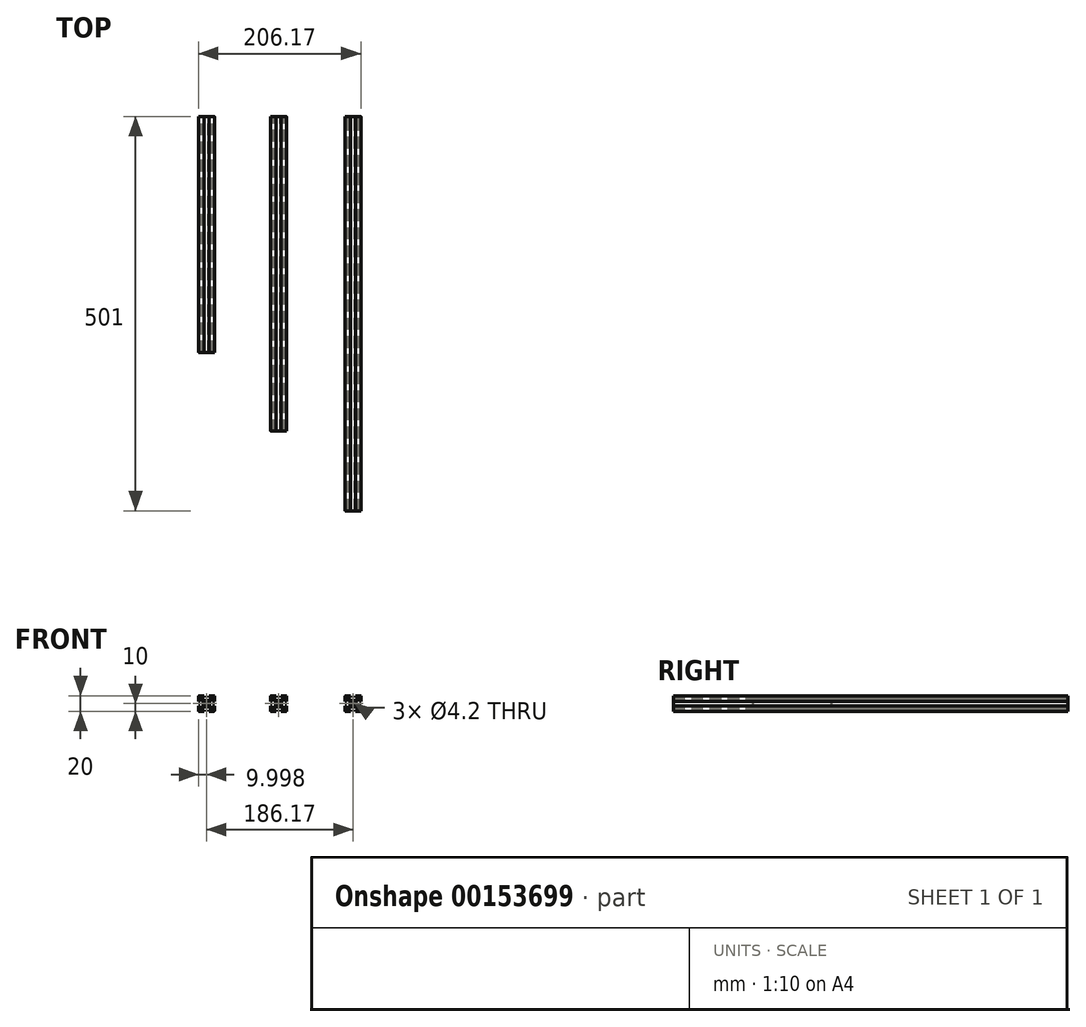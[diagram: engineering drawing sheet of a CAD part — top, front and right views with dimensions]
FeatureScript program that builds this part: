
annotation { "Feature Type Name" : "Feature", "Feature Type Description" : "" }
export const myFeature = defineFeature(function(context is Context, id is Id, definition is map)
    precondition{}
    {
        {
            var Q0;
            Q0=qCreatedBy(makeId("Front.planeOp"),FACE);
            var sketch = newSketch(context, id + "F0", { "sketchPlane" : qUnion([Q0])});
            skCircle(sketch, "E0", {"center": v(0, 0) * mm, "radius": 2.1 * mm});
            skLineSegment(sketch, "E1.bottom", {"start": v(-9.5, 10) * mm, "end": v(-3, 10) * mm});
            skLineSegment(sketch, "E1.top", {"start": v(-5.8, 8) * mm, "end": v(-3, 8) * mm});
            skLineSegment(sketch, "E2.trimOffspring", {"start": v(-3, 10) * mm, "end": v(-9.5, 10) * mm});
            skLineSegment(sketch, "E3.trimOffspring", {"start": v(-3, 8) * mm, "end": v(-3, 10) * mm});
            skLineSegment(sketch, "E4.trimOffspring", {"start": v(-3, 8) * mm, "end": v(-5.8, 8) * mm});
            skArc(sketch, "E5", {"start": v(-9.5, 10) * mm, "mid": v(-9.85, 9.85) * mm, "end": v(-10, 9.5) * mm});
            skArc(sketch, "E6", {"start": v(-5.8, 8) * mm, "mid": v(-6.26, 7.7) * mm, "end": v(-6.15, 7.15) * mm});
            skLineSegment(sketch, "E7", {"start": v(-3, 4) * mm, "end": v(-6.15, 7.15) * mm});
            skLineSegment(sketch, "E8.MirrorCS", {"start": v(-4, 3) * mm, "end": v(-7.15, 6.15) * mm});
            skLineSegment(sketch, "E9.MirrorCS", {"start": v(-8, 5.8) * mm, "end": v(-8, 3) * mm});
            skArc(sketch, "E10.MirrorCS", {"start": v(-8, 5.8) * mm, "mid": v(-7.7, 6.26) * mm, "end": v(-7.15, 6.15) * mm});
            skLineSegment(sketch, "E11.MirrorCS", {"start": v(-8, 3) * mm, "end": v(-10, 3) * mm});
            skLineSegment(sketch, "E12.MirrorCS", {"start": v(-10, 3) * mm, "end": v(-10, 9.5) * mm});
            skLineSegment(sketch, "E13.MirrorCS", {"start": v(-8, 3) * mm, "end": v(-8, 5.8) * mm});
            skLineSegment(sketch, "E14.MirrorCS", {"start": v(9.5, 10) * mm, "end": v(3, 10) * mm});
            skLineSegment(sketch, "E15.MirrorCS", {"start": v(8, 5.8) * mm, "end": v(8, 3) * mm});
            skLineSegment(sketch, "E16.MirrorCS", {"start": v(5.8, 8) * mm, "end": v(3, 8) * mm});
            skLineSegment(sketch, "E17.MirrorCS", {"start": v(3, 4) * mm, "end": v(6.15, 7.15) * mm});
            skLineSegment(sketch, "E18.MirrorCS", {"start": v(8, 3) * mm, "end": v(8, 5.8) * mm});
            skArc(sketch, "E19.MirrorCS", {"start": v(5.8, 8) * mm, "mid": v(6.26, 7.7) * mm, "end": v(6.15, 7.15) * mm});
            skLineSegment(sketch, "E20.MirrorCS", {"start": v(10, 3) * mm, "end": v(10, 9.5) * mm});
            skArc(sketch, "E21.MirrorCS", {"start": v(8, 5.8) * mm, "mid": v(7.7, 6.26) * mm, "end": v(7.15, 6.15) * mm});
            skArc(sketch, "E22.MirrorCS", {"start": v(9.5, 10) * mm, "mid": v(9.85, 9.85) * mm, "end": v(10, 9.5) * mm});
            skLineSegment(sketch, "E23.MirrorCS", {"start": v(4, 3) * mm, "end": v(7.15, 6.15) * mm});
            skLineSegment(sketch, "E24.MirrorCS", {"start": v(8, 3) * mm, "end": v(10, 3) * mm});
            skLineSegment(sketch, "E25.MirrorCS", {"start": v(3, 8) * mm, "end": v(5.8, 8) * mm});
            skLineSegment(sketch, "E26.MirrorCS", {"start": v(3, 8) * mm, "end": v(3, 10) * mm});
            skLineSegment(sketch, "E27.MirrorCS", {"start": v(3, 10) * mm, "end": v(9.5, 10) * mm});
            skLineSegment(sketch, "E28", {"start": v(-3, 4) * mm, "end": v(3, 4) * mm});
            skArc(sketch, "E29.MirrorCS", {"start": v(9.5, -10) * mm, "mid": v(9.85, -9.85) * mm, "end": v(10, -9.5) * mm});
            skLineSegment(sketch, "E30.MirrorCS", {"start": v(8, -3) * mm, "end": v(8, -5.8) * mm});
            skLineSegment(sketch, "E31.MirrorCS", {"start": v(3, -10) * mm, "end": v(9.5, -10) * mm});
            skLineSegment(sketch, "E32.MirrorCS", {"start": v(-8, -3) * mm, "end": v(-8, -5.8) * mm});
            skLineSegment(sketch, "E33.MirrorCS", {"start": v(-9.5, -10) * mm, "end": v(-3, -10) * mm});
            skLineSegment(sketch, "E34.MirrorCS", {"start": v(3, -8) * mm, "end": v(5.8, -8) * mm});
            skLineSegment(sketch, "E35.MirrorCS", {"start": v(-5.8, -8) * mm, "end": v(-3, -8) * mm});
            skArc(sketch, "E36.MirrorCS", {"start": v(-8, -5.8) * mm, "mid": v(-7.7, -6.26) * mm, "end": v(-7.15, -6.15) * mm});
            skLineSegment(sketch, "E37.MirrorCS", {"start": v(-3, -10) * mm, "end": v(-9.5, -10) * mm});
            skLineSegment(sketch, "E38.MirrorCS", {"start": v(5.8, -8) * mm, "end": v(3, -8) * mm});
            skLineSegment(sketch, "E39.MirrorCS", {"start": v(-3, -8) * mm, "end": v(-3, -10) * mm});
            skLineSegment(sketch, "E40.MirrorCS", {"start": v(10, -3) * mm, "end": v(10, -9.5) * mm});
            skLineSegment(sketch, "E41.MirrorCS", {"start": v(-10, -3) * mm, "end": v(-10, -9.5) * mm});
            skLineSegment(sketch, "E42.MirrorCS", {"start": v(-4, -3) * mm, "end": v(-7.15, -6.15) * mm});
            skArc(sketch, "E43.MirrorCS", {"start": v(8, -5.8) * mm, "mid": v(7.7, -6.26) * mm, "end": v(7.15, -6.15) * mm});
            skLineSegment(sketch, "E44.MirrorCS", {"start": v(4, -3) * mm, "end": v(7.15, -6.15) * mm});
            skLineSegment(sketch, "E45.MirrorCS", {"start": v(9.5, -10) * mm, "end": v(3, -10) * mm});
            skArc(sketch, "E46.MirrorCS", {"start": v(-5.8, -8) * mm, "mid": v(-6.26, -7.7) * mm, "end": v(-6.15, -7.15) * mm});
            skArc(sketch, "E47.MirrorCS", {"start": v(5.8, -8) * mm, "mid": v(6.26, -7.7) * mm, "end": v(6.15, -7.15) * mm});
            skArc(sketch, "E48.MirrorCS", {"start": v(-9.5, -10) * mm, "mid": v(-9.85, -9.85) * mm, "end": v(-10, -9.5) * mm});
            skLineSegment(sketch, "E49.MirrorCS", {"start": v(-8, -5.8) * mm, "end": v(-8, -3) * mm});
            skLineSegment(sketch, "E50.MirrorCS", {"start": v(-3, -8) * mm, "end": v(-5.8, -8) * mm});
            skLineSegment(sketch, "E51.MirrorCS", {"start": v(8, -5.8) * mm, "end": v(8, -3) * mm});
            skLineSegment(sketch, "E52.MirrorCS", {"start": v(3, -4) * mm, "end": v(6.15, -7.15) * mm});
            skLineSegment(sketch, "E53.MirrorCS", {"start": v(-3, -4) * mm, "end": v(3, -4) * mm});
            skLineSegment(sketch, "E54.MirrorCS", {"start": v(-3, -4) * mm, "end": v(-6.15, -7.15) * mm});
            skLineSegment(sketch, "E55.MirrorCS", {"start": v(8, -3) * mm, "end": v(10, -3) * mm});
            skLineSegment(sketch, "E56.MirrorCS", {"start": v(-8, -3) * mm, "end": v(-10, -3) * mm});
            skLineSegment(sketch, "E57.MirrorCS", {"start": v(3, -8) * mm, "end": v(3, -10) * mm});
            skLineSegment(sketch, "E58", {"start": v(-4, 3) * mm, "end": v(-4, -3) * mm});
            skLineSegment(sketch, "E59", {"start": v(4, 3) * mm, "end": v(4, -3) * mm});
            skLineSegment(sketch, "E60", {"start": v(-45.77, 47.35) * mm, "end": v(-45.77, -56.41) * mm});
            skLineSegment(sketch, "E61.MirrorCS", {"start": v(-83.53, 3) * mm, "end": v(-83.53, 5.8) * mm});
            skLineSegment(sketch, "E62.MirrorCS", {"start": v(-101.03, 10) * mm, "end": v(-94.53, 10) * mm});
            skLineSegment(sketch, "E63.MirrorCS", {"start": v(-94.53, 8) * mm, "end": v(-94.53, 10) * mm});
            skLineSegment(sketch, "E64.MirrorCS", {"start": v(-99.53, 3) * mm, "end": v(-99.53, 5.8) * mm});
            skLineSegment(sketch, "E65.MirrorCS", {"start": v(-85.74, 8) * mm, "end": v(-88.53, 8) * mm});
            skLineSegment(sketch, "E66.MirrorCS", {"start": v(-88.53, -8) * mm, "end": v(-85.74, -8) * mm});
            skArc(sketch, "E67.MirrorCS", {"start": v(-82.03, -10) * mm, "mid": v(-81.68, -9.85) * mm, "end": v(-81.53, -9.5) * mm});
            skLineSegment(sketch, "E68.MirrorCS", {"start": v(-82.03, 10) * mm, "end": v(-88.53, 10) * mm});
            skLineSegment(sketch, "E69.MirrorCS", {"start": v(-94.53, 8) * mm, "end": v(-97.33, 8) * mm});
            skArc(sketch, "E70.MirrorCS", {"start": v(-97.33, 8) * mm, "mid": v(-97.79, 7.7) * mm, "end": v(-97.68, 7.15) * mm});
            skArc(sketch, "E71.MirrorCS", {"start": v(-101.03, 10) * mm, "mid": v(-101.39, 9.85) * mm, "end": v(-101.53, 9.5) * mm});
            skLineSegment(sketch, "E72.MirrorCS", {"start": v(-81.53, 3) * mm, "end": v(-81.53, 9.5) * mm});
            skLineSegment(sketch, "E73.MirrorCS", {"start": v(-88.53, 10) * mm, "end": v(-82.03, 10) * mm});
            skLineSegment(sketch, "E74.MirrorCS", {"start": v(-83.53, 5.8) * mm, "end": v(-83.53, 3) * mm});
            skArc(sketch, "E75.MirrorCS", {"start": v(-83.53, 5.8) * mm, "mid": v(-83.84, 6.26) * mm, "end": v(-84.38, 6.15) * mm});
            skLineSegment(sketch, "E76.MirrorCS", {"start": v(-83.53, 3) * mm, "end": v(-81.53, 3) * mm});
            skLineSegment(sketch, "E77.MirrorCS", {"start": v(-87.53, 3) * mm, "end": v(-87.53, -3) * mm});
            skLineSegment(sketch, "E78.MirrorCS", {"start": v(-87.53, -3) * mm, "end": v(-84.38, -6.15) * mm});
            skLineSegment(sketch, "E79.MirrorCS", {"start": v(-94.53, 10) * mm, "end": v(-101.03, 10) * mm});
            skLineSegment(sketch, "E80.MirrorCS", {"start": v(-95.53, 3) * mm, "end": v(-98.68, 6.15) * mm});
            skLineSegment(sketch, "E81.MirrorCS", {"start": v(-101.53, 3) * mm, "end": v(-101.53, 9.5) * mm});
            skLineSegment(sketch, "E82.MirrorCS", {"start": v(-88.53, 8) * mm, "end": v(-88.53, 10) * mm});
            skLineSegment(sketch, "E83.MirrorCS", {"start": v(-88.53, 8) * mm, "end": v(-85.74, 8) * mm});
            skArc(sketch, "E84.MirrorCS", {"start": v(-82.03, 10) * mm, "mid": v(-81.68, 9.85) * mm, "end": v(-81.53, 9.5) * mm});
            skArc(sketch, "E85.MirrorCS", {"start": v(-85.74, 8) * mm, "mid": v(-85.28, 7.7) * mm, "end": v(-85.38, 7.15) * mm});
            skLineSegment(sketch, "E86.MirrorCS", {"start": v(-87.53, 3) * mm, "end": v(-84.38, 6.15) * mm});
            skLineSegment(sketch, "E87.MirrorCS", {"start": v(-83.53, -3) * mm, "end": v(-81.53, -3) * mm});
            skArc(sketch, "E88.MirrorCS", {"start": v(-99.53, 5.8) * mm, "mid": v(-99.22, 6.26) * mm, "end": v(-98.68, 6.15) * mm});
            skLineSegment(sketch, "E89.MirrorCS", {"start": v(-88.53, 4) * mm, "end": v(-85.38, 7.15) * mm});
            skLineSegment(sketch, "E90.MirrorCS", {"start": v(-97.33, 8) * mm, "end": v(-94.53, 8) * mm});
            skLineSegment(sketch, "E91.MirrorCS", {"start": v(-85.74, -8) * mm, "end": v(-88.53, -8) * mm});
            skLineSegment(sketch, "E92.MirrorCS", {"start": v(-99.53, 5.8) * mm, "end": v(-99.53, 3) * mm});
            skLineSegment(sketch, "E93.MirrorCS", {"start": v(-83.53, -3) * mm, "end": v(-83.53, -5.8) * mm});
            skLineSegment(sketch, "E94.MirrorCS", {"start": v(-94.53, 4) * mm, "end": v(-97.68, 7.15) * mm});
            skLineSegment(sketch, "E95.MirrorCS", {"start": v(-88.53, -10) * mm, "end": v(-82.03, -10) * mm});
            skLineSegment(sketch, "E96.MirrorCS", {"start": v(-94.53, -8) * mm, "end": v(-94.53, -10) * mm});
            skLineSegment(sketch, "E97.MirrorCS", {"start": v(-94.53, -8) * mm, "end": v(-97.33, -8) * mm});
            skLineSegment(sketch, "E98.MirrorCS", {"start": v(-95.53, 3) * mm, "end": v(-95.53, -3) * mm});
            skArc(sketch, "E99.MirrorCS", {"start": v(-99.53, -5.8) * mm, "mid": v(-99.22, -6.26) * mm, "end": v(-98.68, -6.15) * mm});
            skLineSegment(sketch, "E100.MirrorCS", {"start": v(-99.53, -3) * mm, "end": v(-101.53, -3) * mm});
            skLineSegment(sketch, "E101.MirrorCS", {"start": v(-88.53, -8) * mm, "end": v(-88.53, -10) * mm});
            skArc(sketch, "E102.MirrorCS", {"start": v(-101.03, -10) * mm, "mid": v(-101.39, -9.85) * mm, "end": v(-101.53, -9.5) * mm});
            skArc(sketch, "E103.MirrorCS", {"start": v(-83.53, -5.8) * mm, "mid": v(-83.84, -6.26) * mm, "end": v(-84.38, -6.15) * mm});
            skArc(sketch, "E104.MirrorCS", {"start": v(-97.33, -8) * mm, "mid": v(-97.79, -7.7) * mm, "end": v(-97.68, -7.15) * mm});
            skLineSegment(sketch, "E105.MirrorCS", {"start": v(-82.03, -10) * mm, "end": v(-88.53, -10) * mm});
            skArc(sketch, "E106.MirrorCS", {"start": v(-85.74, -8) * mm, "mid": v(-85.28, -7.7) * mm, "end": v(-85.38, -7.15) * mm});
            skLineSegment(sketch, "E107.MirrorCS", {"start": v(-81.53, -3) * mm, "end": v(-81.53, -9.5) * mm});
            skLineSegment(sketch, "E108.MirrorCS", {"start": v(-99.53, -5.8) * mm, "end": v(-99.53, -3) * mm});
            skLineSegment(sketch, "E109.MirrorCS", {"start": v(-83.53, -5.8) * mm, "end": v(-83.53, -3) * mm});
            skLineSegment(sketch, "E110.MirrorCS", {"start": v(-88.53, -4) * mm, "end": v(-85.38, -7.15) * mm});
            skLineSegment(sketch, "E111.MirrorCS", {"start": v(-99.53, 3) * mm, "end": v(-101.53, 3) * mm});
            skLineSegment(sketch, "E112.MirrorCS", {"start": v(-94.53, -4) * mm, "end": v(-97.68, -7.15) * mm});
            skCircle(sketch, "E113.MirrorC", {"center": v(-91.53, 0) * mm, "radius": 2.1 * mm});
            skLineSegment(sketch, "E114.MirrorCS", {"start": v(-97.33, -8) * mm, "end": v(-94.53, -8) * mm});
            skLineSegment(sketch, "E115.MirrorCS", {"start": v(-101.53, -3) * mm, "end": v(-101.53, -9.5) * mm});
            skLineSegment(sketch, "E116.MirrorCS", {"start": v(-88.53, -4) * mm, "end": v(-94.53, -4) * mm});
            skLineSegment(sketch, "E117.MirrorCS", {"start": v(-99.53, -3) * mm, "end": v(-99.53, -5.8) * mm});
            skLineSegment(sketch, "E118.MirrorCS", {"start": v(-88.53, 4) * mm, "end": v(-94.53, 4) * mm});
            skLineSegment(sketch, "E119.MirrorCS", {"start": v(-94.53, -10) * mm, "end": v(-101.03, -10) * mm});
            skLineSegment(sketch, "E120.MirrorCS", {"start": v(-101.03, -10) * mm, "end": v(-94.53, -10) * mm});
            skLineSegment(sketch, "E121.MirrorCS", {"start": v(-95.53, -3) * mm, "end": v(-98.68, -6.15) * mm});
            skLineSegment(sketch, "E122", {"start": v(47.32, 47.35) * mm, "end": v(47.32, -56.41) * mm});
            skLineSegment(sketch, "E123.MirrorCS", {"start": v(97.64, -8) * mm, "end": v(100.43, -8) * mm});
            skLineSegment(sketch, "E124.MirrorCS", {"start": v(91.64, -8) * mm, "end": v(91.64, -10) * mm});
            skLineSegment(sketch, "E125.MirrorCS", {"start": v(86.64, 3) * mm, "end": v(86.64, 5.8) * mm});
            skArc(sketch, "E126.MirrorCS", {"start": v(88.84, 8) * mm, "mid": v(88.38, 7.7) * mm, "end": v(88.5, 7.15) * mm});
            skLineSegment(sketch, "E127.MirrorCS", {"start": v(91.64, 10) * mm, "end": v(85.14, 10) * mm});
            skArc(sketch, "E128.MirrorCS", {"start": v(102.64, -5.8) * mm, "mid": v(102.33, -6.26) * mm, "end": v(101.79, -6.15) * mm});
            skLineSegment(sketch, "E129.MirrorCS", {"start": v(102.64, 3) * mm, "end": v(102.64, 5.8) * mm});
            skLineSegment(sketch, "E130.MirrorCS", {"start": v(100.43, 8) * mm, "end": v(97.64, 8) * mm});
            skLineSegment(sketch, "E131.MirrorCS", {"start": v(91.64, 8) * mm, "end": v(88.84, 8) * mm});
            skLineSegment(sketch, "E132.MirrorCS", {"start": v(91.64, 8) * mm, "end": v(91.64, 10) * mm});
            skLineSegment(sketch, "E133.MirrorCS", {"start": v(100.43, -8) * mm, "end": v(97.64, -8) * mm});
            skArc(sketch, "E134.MirrorCS", {"start": v(86.64, 5.8) * mm, "mid": v(86.95, 6.26) * mm, "end": v(87.5, 6.15) * mm});
            skLineSegment(sketch, "E135.MirrorCS", {"start": v(102.64, -3) * mm, "end": v(102.64, -5.8) * mm});
            skLineSegment(sketch, "E136.MirrorCS", {"start": v(86.64, -5.8) * mm, "end": v(86.64, -3) * mm});
            skArc(sketch, "E137.MirrorCS", {"start": v(86.64, -5.8) * mm, "mid": v(86.95, -6.26) * mm, "end": v(87.5, -6.15) * mm});
            skLineSegment(sketch, "E138.MirrorCS", {"start": v(84.64, 3) * mm, "end": v(84.64, 9.5) * mm});
            skLineSegment(sketch, "E139.MirrorCS", {"start": v(85.14, -10) * mm, "end": v(91.64, -10) * mm});
            skArc(sketch, "E140.MirrorCS", {"start": v(85.14, -10) * mm, "mid": v(84.78, -9.85) * mm, "end": v(84.64, -9.5) * mm});
            skArc(sketch, "E141.MirrorCS", {"start": v(100.43, -8) * mm, "mid": v(100.9, -7.7) * mm, "end": v(100.79, -7.15) * mm});
            skLineSegment(sketch, "E142.MirrorCS", {"start": v(97.64, -10) * mm, "end": v(104.14, -10) * mm});
            skLineSegment(sketch, "E143.MirrorCS", {"start": v(85.14, 10) * mm, "end": v(91.64, 10) * mm});
            skLineSegment(sketch, "E144.MirrorCS", {"start": v(97.64, 8) * mm, "end": v(100.43, 8) * mm});
            skArc(sketch, "E145.MirrorCS", {"start": v(100.43, 8) * mm, "mid": v(100.9, 7.7) * mm, "end": v(100.79, 7.15) * mm});
            skLineSegment(sketch, "E146.MirrorCS", {"start": v(97.64, 4) * mm, "end": v(100.79, 7.15) * mm});
            skArc(sketch, "E147.MirrorCS", {"start": v(102.64, 5.8) * mm, "mid": v(102.33, 6.26) * mm, "end": v(101.79, 6.15) * mm});
            skLineSegment(sketch, "E148.MirrorCS", {"start": v(102.64, 3) * mm, "end": v(104.64, 3) * mm});
            skArc(sketch, "E149.MirrorCS", {"start": v(85.14, 10) * mm, "mid": v(84.78, 9.85) * mm, "end": v(84.64, 9.5) * mm});
            skLineSegment(sketch, "E150.MirrorCS", {"start": v(86.64, 5.8) * mm, "end": v(86.64, 3) * mm});
            skArc(sketch, "E151.MirrorCS", {"start": v(104.14, -10) * mm, "mid": v(104.5, -9.85) * mm, "end": v(104.64, -9.5) * mm});
            skLineSegment(sketch, "E152.MirrorCS", {"start": v(86.64, 3) * mm, "end": v(84.64, 3) * mm});
            skLineSegment(sketch, "E153.MirrorCS", {"start": v(91.64, 4) * mm, "end": v(88.5, 7.15) * mm});
            skLineSegment(sketch, "E154.MirrorCS", {"start": v(91.64, -8) * mm, "end": v(88.84, -8) * mm});
            skLineSegment(sketch, "E155.MirrorCS", {"start": v(98.64, 3) * mm, "end": v(98.64, -3) * mm});
            skLineSegment(sketch, "E156.MirrorCS", {"start": v(98.64, -3) * mm, "end": v(101.79, -6.15) * mm});
            skLineSegment(sketch, "E157.MirrorCS", {"start": v(90.64, -3) * mm, "end": v(87.5, -6.15) * mm});
            skLineSegment(sketch, "E158.MirrorCS", {"start": v(104.64, 3) * mm, "end": v(104.64, 9.5) * mm});
            skLineSegment(sketch, "E159.MirrorCS", {"start": v(104.14, 10) * mm, "end": v(97.64, 10) * mm});
            skLineSegment(sketch, "E160.MirrorCS", {"start": v(98.64, 3) * mm, "end": v(101.79, 6.15) * mm});
            skLineSegment(sketch, "E161.MirrorCS", {"start": v(102.64, 5.8) * mm, "end": v(102.64, 3) * mm});
            skLineSegment(sketch, "E162.MirrorCS", {"start": v(97.64, -4) * mm, "end": v(100.79, -7.15) * mm});
            skLineSegment(sketch, "E163.MirrorCS", {"start": v(97.64, -8) * mm, "end": v(97.64, -10) * mm});
            skLineSegment(sketch, "E164.MirrorCS", {"start": v(90.64, 3) * mm, "end": v(87.5, 6.15) * mm});
            skLineSegment(sketch, "E165.MirrorCS", {"start": v(88.84, 8) * mm, "end": v(91.64, 8) * mm});
            skLineSegment(sketch, "E166.MirrorCS", {"start": v(102.64, -5.8) * mm, "end": v(102.64, -3) * mm});
            skLineSegment(sketch, "E167.MirrorCS", {"start": v(90.64, 3) * mm, "end": v(90.64, -3) * mm});
            skLineSegment(sketch, "E168.MirrorCS", {"start": v(91.64, -4) * mm, "end": v(88.5, -7.15) * mm});
            skLineSegment(sketch, "E169.MirrorCS", {"start": v(97.64, -4) * mm, "end": v(91.64, -4) * mm});
            skLineSegment(sketch, "E170.MirrorCS", {"start": v(86.64, -3) * mm, "end": v(86.64, -5.8) * mm});
            skCircle(sketch, "E171.MirrorC", {"center": v(94.64, 0) * mm, "radius": 2.1 * mm});
            skArc(sketch, "E172.MirrorCS", {"start": v(104.14, 10) * mm, "mid": v(104.5, 9.85) * mm, "end": v(104.64, 9.5) * mm});
            skArc(sketch, "E173.MirrorCS", {"start": v(88.84, -8) * mm, "mid": v(88.38, -7.7) * mm, "end": v(88.5, -7.15) * mm});
            skLineSegment(sketch, "E174.MirrorCS", {"start": v(91.64, -10) * mm, "end": v(85.14, -10) * mm});
            skLineSegment(sketch, "E175.MirrorCS", {"start": v(86.64, -3) * mm, "end": v(84.64, -3) * mm});
            skLineSegment(sketch, "E176.MirrorCS", {"start": v(104.64, -3) * mm, "end": v(104.64, -9.5) * mm});
            skLineSegment(sketch, "E177.MirrorCS", {"start": v(97.64, 4) * mm, "end": v(91.64, 4) * mm});
            skLineSegment(sketch, "E178.MirrorCS", {"start": v(97.64, 10) * mm, "end": v(104.14, 10) * mm});
            skLineSegment(sketch, "E179.MirrorCS", {"start": v(97.64, 8) * mm, "end": v(97.64, 10) * mm});
            skLineSegment(sketch, "E180.MirrorCS", {"start": v(88.84, -8) * mm, "end": v(91.64, -8) * mm});
            skLineSegment(sketch, "E181.MirrorCS", {"start": v(102.64, -3) * mm, "end": v(104.64, -3) * mm});
            skLineSegment(sketch, "E182.MirrorCS", {"start": v(84.64, -3) * mm, "end": v(84.64, -9.5) * mm});
            skLineSegment(sketch, "E183.MirrorCS", {"start": v(104.14, -10) * mm, "end": v(97.64, -10) * mm});
            skSolve(sketch);
        }
        {
            var Q0;
            Q0=makeQuery(id+"F0.imprint","IMPRINT",FACE,{"disambiguationData":[TD([[makeQuery(id+"F0.imprint","IMPRINT",EDGE,{"derivedFrom":sQuery(id+"F0.wireOp",EDGE,"E0")}),-1.0]])]});
            extrude(context, id + "F1", {"entities" : qUnion([Q0]), "depth" : 400 * mm});
        }
        {
            var Q0;
            Q0=makeQuery(id+"F0.imprint","IMPRINT",FACE,{"disambiguationData":[TD([[makeQuery(id+"F0.imprint","IMPRINT",EDGE,{"derivedFrom":sQuery(id+"F0.wireOp",EDGE,"E63.MirrorCS")}),1.0]])]});
            extrude(context, id + "F2", {"entities" : qUnion([Q0]), "depth" : 300 * mm});
        }
        {
            var Q0;
            Q0=makeQuery(id+"F0.imprint","IMPRINT",FACE,{"disambiguationData":[TD([[makeQuery(id+"F0.imprint","IMPRINT",EDGE,{"derivedFrom":sQuery(id+"F0.wireOp",EDGE,"E124.MirrorCS")}),-1.0]])]});
            extrude(context, id + "F3", {"entities" : qUnion([Q0]), "depth" : 501 * mm});
        }
    });
